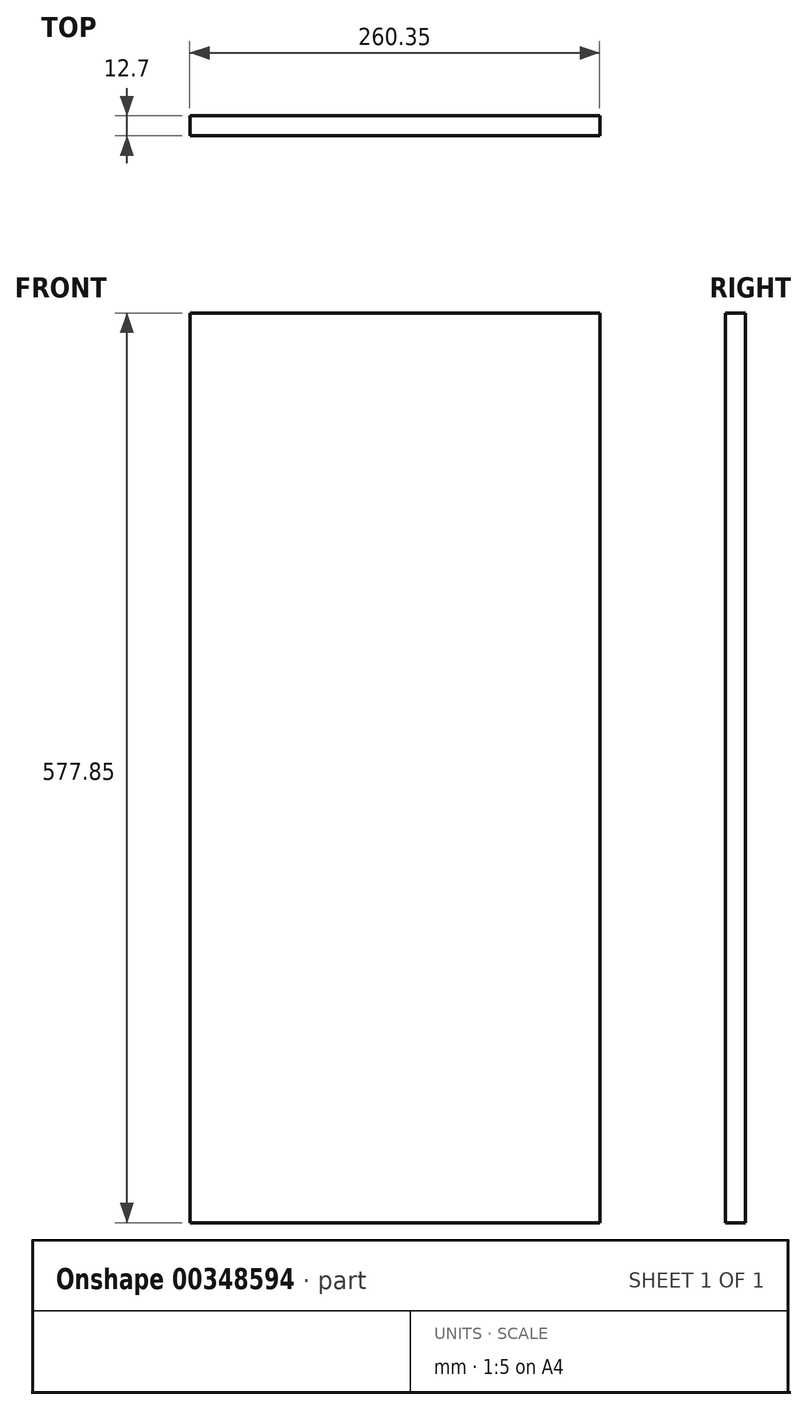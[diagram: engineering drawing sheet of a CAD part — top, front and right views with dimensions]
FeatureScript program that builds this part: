
annotation { "Feature Type Name" : "Feature", "Feature Type Description" : "" }
export const myFeature = defineFeature(function(context is Context, id is Id, definition is map)
    precondition{}
    {
        {
            var Q0;
            Q0=qCreatedBy(makeId("Top.planeOp"),FACE);
            var sketch = newSketch(context, id + "F0", { "sketchPlane" : qUnion([Q0])});
            skLineSegment(sketch, "E0.bottom", {"start": v(-128.23, -26.68) * mm, "end": v(132.12, -26.68) * mm});
            skLineSegment(sketch, "E0.top", {"start": v(-128.23, -39.38) * mm, "end": v(132.12, -39.38) * mm});
            skLineSegment(sketch, "E0.left", {"start": v(-128.23, -26.68) * mm, "end": v(-128.23, -39.38) * mm});
            skLineSegment(sketch, "E0.right", {"start": v(132.12, -26.68) * mm, "end": v(132.12, -39.38) * mm});
            skSolve(sketch);
        }
        {
            var Q0;
            Q0 = qSketchRegion(id + "F0", true);
            extrude(context, id + "F1", {"entities" : qUnion([Q0]), "depth" : 577.85 * mm});
        }
    });
